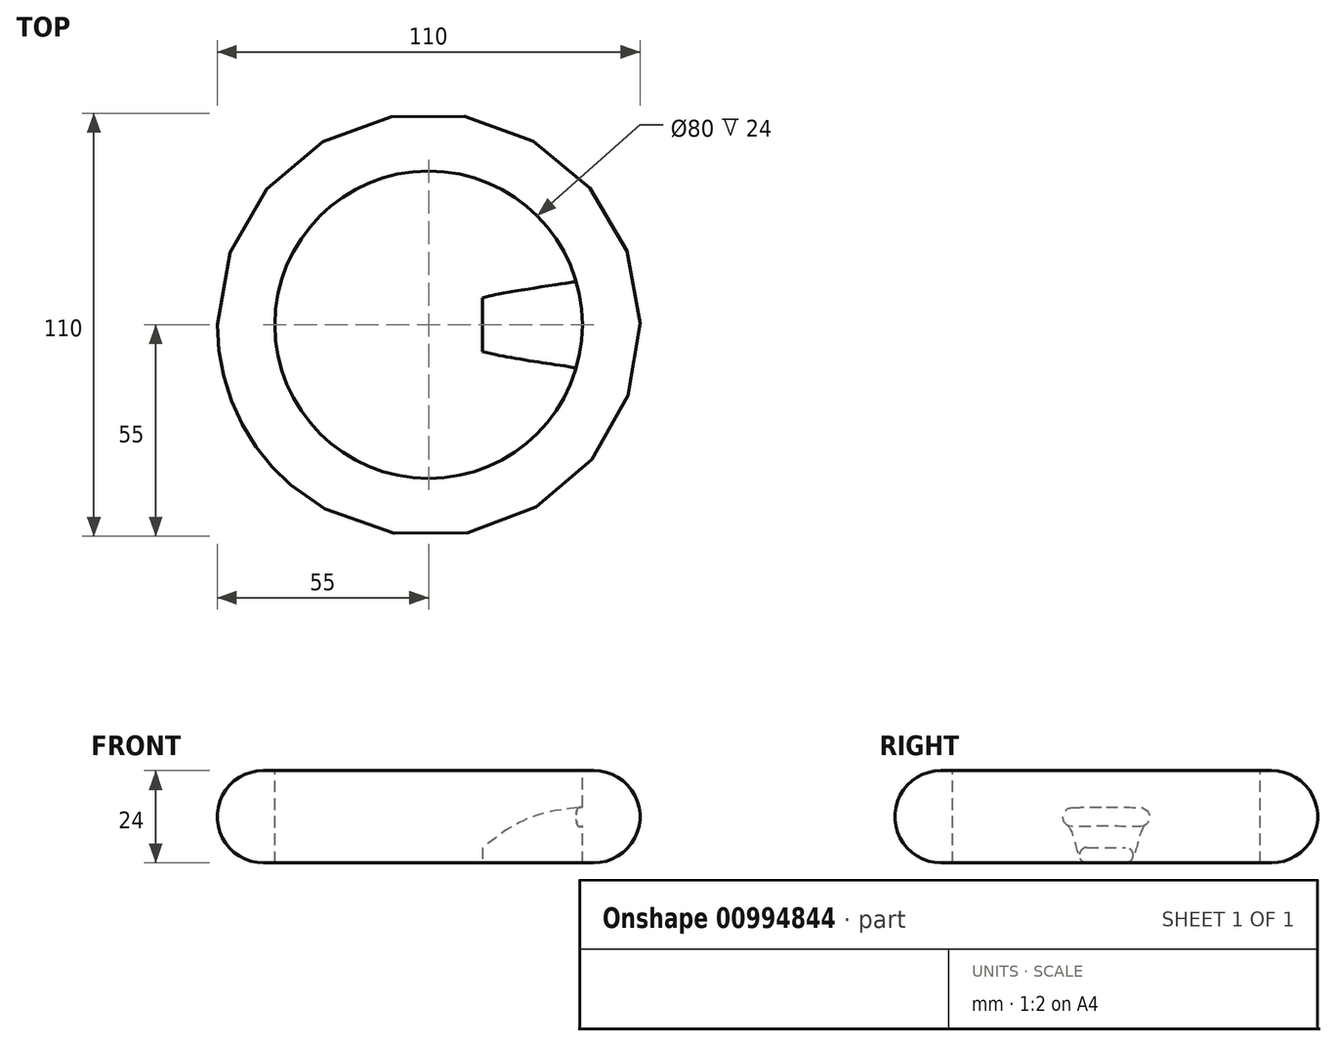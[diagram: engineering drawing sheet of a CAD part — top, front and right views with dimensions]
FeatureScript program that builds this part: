
annotation { "Feature Type Name" : "Feature", "Feature Type Description" : "" }
export const myFeature = defineFeature(function(context is Context, id is Id, definition is map)
    precondition{}
    {
        {
            var Q0;
            Q0=qCreatedBy(makeId("Top.planeOp"),FACE);
            var sketch = newSketch(context, id + "F0", { "sketchPlane" : qUnion([Q0])});
            skCircle(sketch, "E0", {"center": v(0, 0) * mm, "radius": 40 * mm});
            skSolve(sketch);
        }
        {
            var Q0;
            Q0=qCreatedBy(makeId("Front.planeOp"),FACE);
            var sketch = newSketch(context, id + "F1", { "sketchPlane" : qUnion([Q0])});
            skArc(sketch, "E1", {"start": v(-43, 12) * mm, "mid": v(-55, 0) * mm, "end": v(-43, -12) * mm});
            skLineSegment(sketch, "E2", {"start": v(-43, 12) * mm, "end": v(-40, 12) * mm});
            skLineSegment(sketch, "E3", {"start": v(-43, -12) * mm, "end": v(-40, -12) * mm});
            skLineSegment(sketch, "E4", {"start": v(-40, 12) * mm, "end": v(-40, -12) * mm});
            skSolve(sketch);
        }
        {
            var Q0;
            Q0=makeQuery(id+"F1.imprint","IMPRINT",FACE,{"disambiguationData":[TD([[makeQuery(id+"F1.imprint","IMPRINT",EDGE,{"derivedFrom":sQuery(id+"F1.wireOp",EDGE,"E1")}),1.0]])]});
            var Q1;
            Q1=sQuery(id+"F0.wireOp",EDGE,"E0");
            sweep(context, id + "F2", {"profiles" : qUnion([Q0]), "path" : qUnion([Q1])});
        }
        {
            var Q0;
            Q0=qCreatedBy(makeId("Right.planeOp"),FACE);
            cPlane(context, id + "F3", {"entities" : qUnion([Q0]), "cplaneType" : CPlaneType.OFFSET, "offset" : 40 * mm, "width" : 150 * mm, "height" : 150 * mm});
        }
        {
            var Q0;
            Q0=qCreatedBy(id+"F3.planeOp",FACE);
            var sketch = newSketch(context, id + "F4", { "sketchPlane" : qUnion([Q0])});
            skLineSegment(sketch, "E5", {"start": v(-9, 0) * mm, "end": v(9, 0) * mm});
            skArc(sketch, "E6.0.startCap", {"start": v(-9, -2.5) * mm, "mid": v(-11.5, 0) * mm, "end": v(-9, 2.5) * mm});
            skArc(sketch, "E6.0.endCap", {"start": v(9, 2.5) * mm, "mid": v(11.5, 0) * mm, "end": v(9, -2.5) * mm});
            skLineSegment(sketch, "E6.0.left", {"start": v(-9, 2.5) * mm, "end": v(9, 2.5) * mm});
            skLineSegment(sketch, "E6.0.right", {"start": v(-9, -2.5) * mm, "end": v(9, -2.5) * mm});
            skSolve(sketch);
        }
        {
            var Q0;
            Q0=qCreatedBy(makeId("Right.planeOp"),FACE);
            cPlane(context, id + "F5", {"entities" : qUnion([Q0]), "cplaneType" : CPlaneType.OFFSET, "offset" : 14 * mm, "width" : 150 * mm, "height" : 150 * mm});
        }
        {
            var Q0;
            Q0=qCreatedBy(id+"F5.planeOp",FACE);
            var sketch = newSketch(context, id + "F6", { "sketchPlane" : qUnion([Q0])});
            skLineSegment(sketch, "E7", {"start": v(-5, -10) * mm, "end": v(5, -10) * mm});
            skArc(sketch, "E8.0.startCap", {"start": v(-5, -12) * mm, "mid": v(-7, -10) * mm, "end": v(-5, -8) * mm});
            skArc(sketch, "E8.0.endCap", {"start": v(5, -8) * mm, "mid": v(7, -10) * mm, "end": v(5, -12) * mm});
            skLineSegment(sketch, "E8.0.left", {"start": v(-5, -8) * mm, "end": v(5, -8) * mm});
            skLineSegment(sketch, "E8.0.right", {"start": v(-5, -12) * mm, "end": v(5, -12) * mm});
            skSolve(sketch);
        }
        {
            var Q0;
            Q0=qCreatedBy(makeId("Front.planeOp"),FACE);
            var sketch = newSketch(context, id + "F7", { "sketchPlane" : qUnion([Q0])});
            skFitSpline(sketch, "E9", {"points": [v(14, -12) * mm, v(17.36, -10.57) * mm, v(19.73, -8.95) * mm, v(25.94, -5.3) * mm, v(34.78, -2.93) * mm, v(37.7, -2.65) * mm, v(40, -2.5) * mm], "startDerivative": vector(23.36, 2.46) * mm, "endDerivative": vector(25.77, 2.82) * mm});
            skSolve(sketch);
        }
        {
            var Q0;
            Q0=qConstructionFilter(qBodyType(qCreatedBy(id+"F7",EDGE),BodyType.WIRE),ConstructionObject.NO);
            var Q2;
            Q2=qSketchRegion(id+"F4",true);
            var Q3;
            Q3=qSketchRegion(id+"F6",true);
            loft(context, id + "F8", {"operationType" : NewBodyOperationType.ADD, "addSections" : true, "spine" : qUnion([Q0]), "sectionCount" : 5, "sheetProfilesArray" : [{ "sheetProfileEntities" : qUnion([Q2]) }, { "sheetProfileEntities" : qUnion([Q3]) }]});
        }
    });
